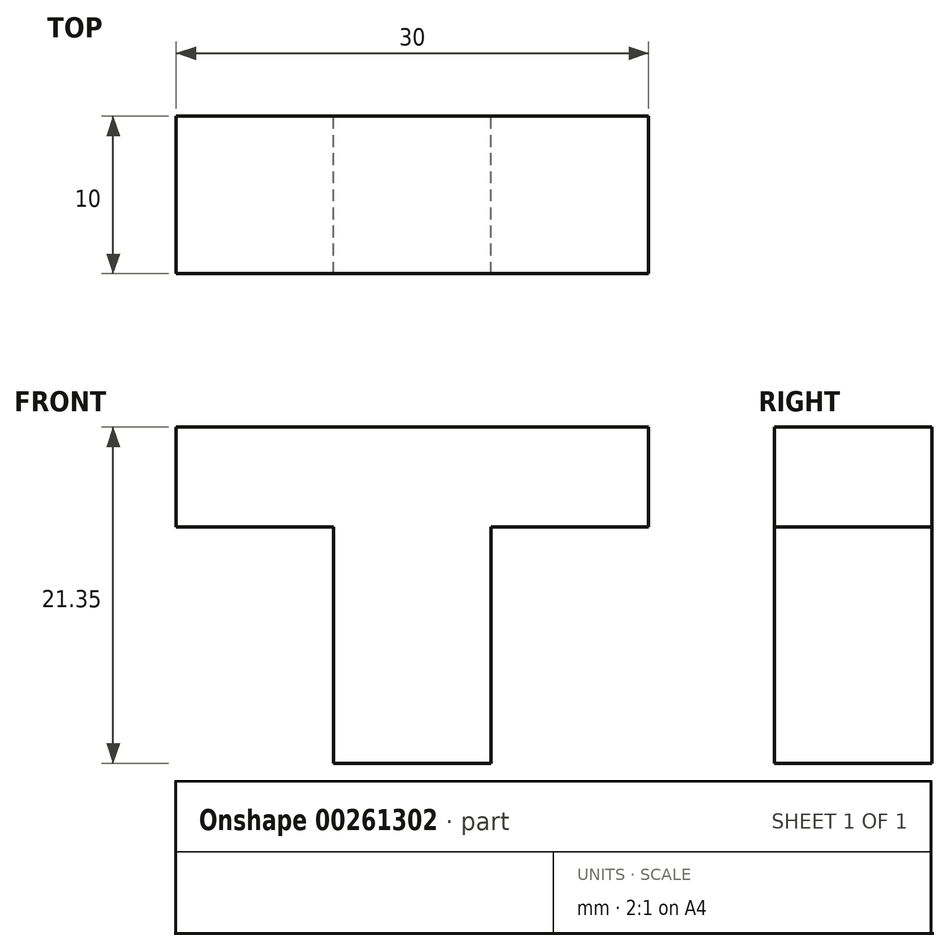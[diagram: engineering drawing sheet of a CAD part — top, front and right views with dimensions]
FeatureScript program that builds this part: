
annotation { "Feature Type Name" : "Feature", "Feature Type Description" : "" }
export const myFeature = defineFeature(function(context is Context, id is Id, definition is map)
    precondition{}
    {
        {
            var Q0;
            Q0=qCreatedBy(makeId("Front.planeOp"),FACE);
            var sketch = newSketch(context, id + "F0", { "sketchPlane" : qUnion([Q0])});
            skLineSegment(sketch, "E0", {"start": v(0, 0) * mm, "end": v(-14.81, 0) * mm});
            skLineSegment(sketch, "E1", {"start": v(-14.81, 0) * mm, "end": v(-14.81, -6.35) * mm});
            skLineSegment(sketch, "E2", {"start": v(-14.81, -6.35) * mm, "end": v(-4.81, -6.35) * mm});
            skLineSegment(sketch, "E3", {"start": v(-4.81, -6.35) * mm, "end": v(-4.81, -21.35) * mm});
            skLineSegment(sketch, "E4", {"start": v(-4.81, -21.35) * mm, "end": v(5.19, -21.35) * mm});
            skLineSegment(sketch, "E5", {"start": v(5.19, -21.35) * mm, "end": v(5.19, -6.35) * mm});
            skLineSegment(sketch, "E6", {"start": v(5.19, -6.35) * mm, "end": v(15.19, -6.35) * mm});
            skPoint(sketch, "E6.endSnap0", {"position": v(-9.81, -6.35) * mm});
            skLineSegment(sketch, "E7", {"start": v(15.19, -6.35) * mm, "end": v(15.19, 0) * mm});
            skLineSegment(sketch, "E8", {"start": v(15.19, 0) * mm, "end": v(0, 0) * mm});
            skSolve(sketch);
        }
        {
            var Q0;
            Q0 = qSketchRegion(id + "F0", true);
            extrude(context, id + "F1", {"entities" : qUnion([Q0]), "depth" : 10 * mm});
        }
    });
